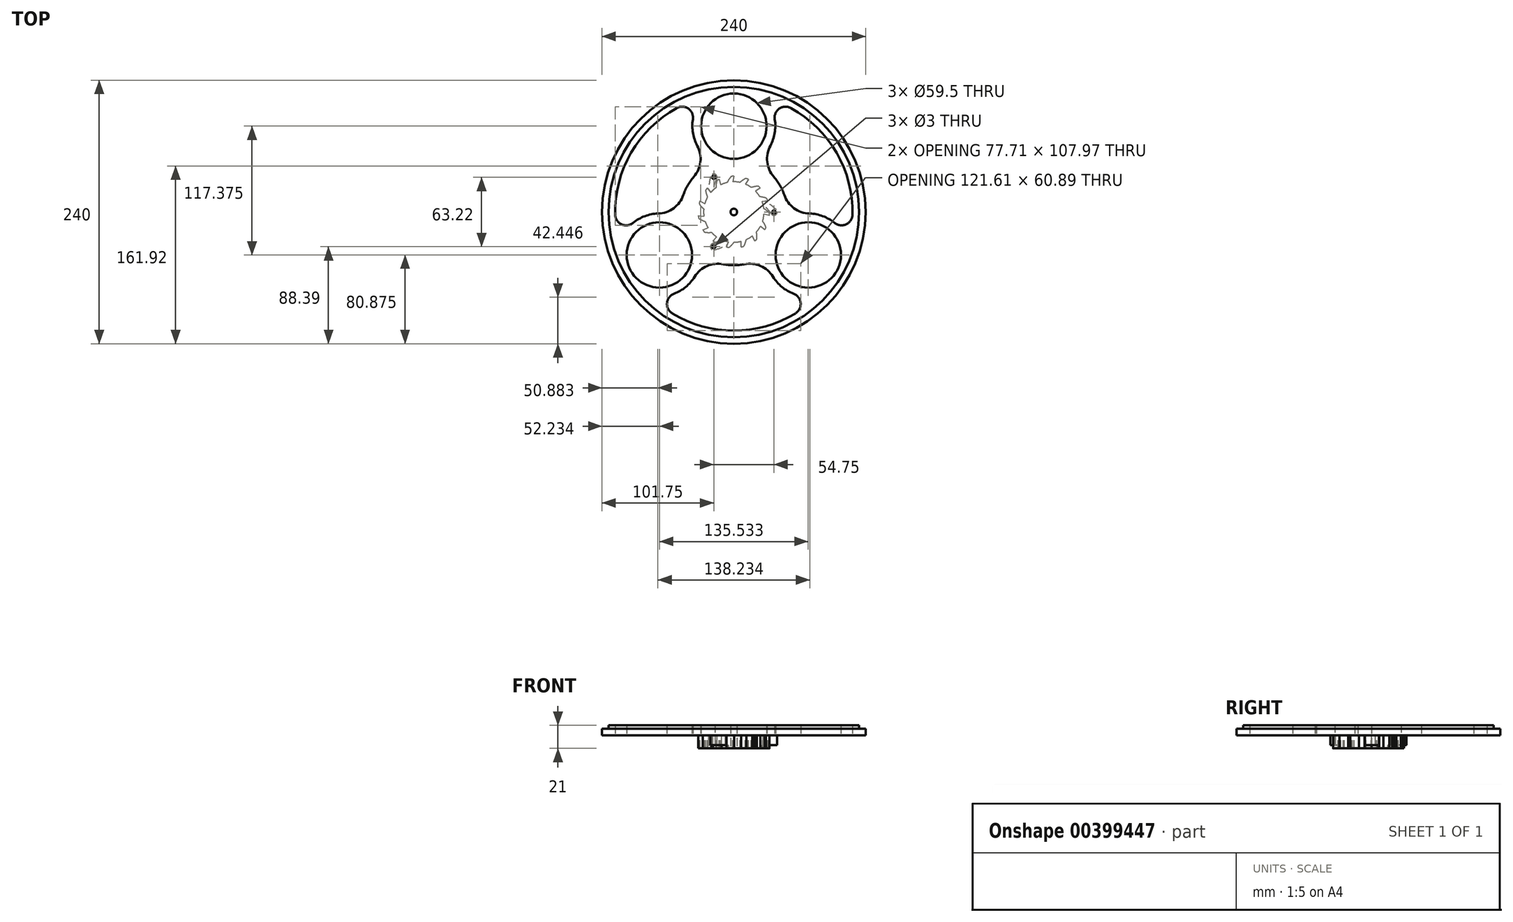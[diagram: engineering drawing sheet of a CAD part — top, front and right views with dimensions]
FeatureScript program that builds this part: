
annotation { "Feature Type Name" : "Feature", "Feature Type Description" : "" }
export const myFeature = defineFeature(function(context is Context, id is Id, definition is map)
    precondition{}
    {
        {
            var Q0;
            Q0=qCreatedBy(makeId("Top.planeOp"),FACE);
            var sketch = newSketch(context, id + "F0", { "sketchPlane" : qUnion([Q0])});
            skCircle(sketch, "E0", {"center": v(0, 0) * mm, "radius": 120 * mm});
            skArc(sketch, "E1", {"start": v(-36.45, 32) * mm, "mid": v(-42, 24.25) * mm, "end": v(-45.93, 15.57) * mm});
            skArc(sketch, "E2", {"start": v(-51.94, 94.7) * mm, "mid": v(-93.53, 54) * mm, "end": v(-107.97, -2.37) * mm});
            skCircle(sketch, "E3", {"center": v(0, 78.25) * mm, "radius": 29.75 * mm});
            skCircle(sketch, "E4", {"center": v(67.77, -39.12) * mm, "radius": 29.75 * mm});
            skCircle(sketch, "E5", {"center": v(-67.77, -39.13) * mm, "radius": 29.75 * mm});
            skLineSegment(sketch, "E6", {"start": v(0, 78.25) * mm, "end": v(-67.77, -39.13) * mm, "construction": true});
            skLineSegment(sketch, "E7", {"start": v(-67.77, -39.13) * mm, "end": v(67.77, -39.12) * mm, "construction": true});
            skLineSegment(sketch, "E8", {"start": v(67.77, -39.12) * mm, "end": v(0, 78.25) * mm, "construction": true});
            skArc(sketch, "E9", {"start": v(-37.26, 84.32) * mm, "mid": v(-37.23, 72) * mm, "end": v(-33.23, 60.34) * mm});
            skArc(sketch, "E10", {"start": v(-68.87, -1.4) * mm, "mid": v(-80.97, -3.76) * mm, "end": v(-91.65, -9.9) * mm});
            skArc(sketch, "E11", {"start": v(35.64, -58.95) * mm, "mid": v(43.74, -68.24) * mm, "end": v(54.4, -74.43) * mm});
            skArc(sketch, "E12.trimOffspring", {"start": v(33.23, 60.34) * mm, "mid": v(37.23, 72) * mm, "end": v(37.26, 84.32) * mm});
            skArc(sketch, "E13.trimOffspring", {"start": v(45.93, 15.57) * mm, "mid": v(42, 24.25) * mm, "end": v(36.45, 32) * mm});
            skArc(sketch, "E14.trimOffspring", {"start": v(-9.48, -47.56) * mm, "mid": v(0, -48.5) * mm, "end": v(9.48, -47.56) * mm});
            skArc(sketch, "E15.trimOffspring", {"start": v(-56.04, -92.33) * mm, "mid": v(0, -108) * mm, "end": v(56.04, -92.33) * mm});
            skArc(sketch, "E16.trimOffspring", {"start": v(-54.4, -74.43) * mm, "mid": v(-43.74, -68.24) * mm, "end": v(-35.64, -58.95) * mm});
            skArc(sketch, "E17.trimOffspring", {"start": v(107.97, -2.37) * mm, "mid": v(93.53, 54) * mm, "end": v(51.94, 94.7) * mm});
            skArc(sketch, "E18.trimOffspring", {"start": v(91.65, -9.9) * mm, "mid": v(80.97, -3.76) * mm, "end": v(68.87, -1.4) * mm});
            skPoint(sketch, "E19.visualSharp", {"position": v(-27.08, 104.55) * mm});
            skArc(sketch, "E19.filletArc", {"start": v(-37.26, 84.32) * mm, "mid": v(-41.36, 94.09) * mm, "end": v(-51.94, 94.7) * mm});
            skPoint(sketch, "E20.visualSharp", {"position": v(-104.08, -28.82) * mm});
            skArc(sketch, "E20.filletArc", {"start": v(-107.97, -2.37) * mm, "mid": v(-102.16, -11.23) * mm, "end": v(-91.65, -9.9) * mm});
            skPoint(sketch, "E21.visualSharp", {"position": v(27.08, 104.55) * mm});
            skArc(sketch, "E21.filletArc", {"start": v(51.94, 94.7) * mm, "mid": v(41.36, 94.09) * mm, "end": v(37.26, 84.32) * mm});
            skPoint(sketch, "E22.visualSharp", {"position": v(104.08, -28.82) * mm});
            skArc(sketch, "E22.filletArc", {"start": v(91.65, -9.9) * mm, "mid": v(102.16, -11.23) * mm, "end": v(107.97, -2.37) * mm});
            skPoint(sketch, "E23.visualSharp", {"position": v(77, -75.73) * mm});
            skArc(sketch, "E23.filletArc", {"start": v(56.04, -92.33) * mm, "mid": v(60.8, -82.86) * mm, "end": v(54.4, -74.43) * mm});
            skPoint(sketch, "E24.visualSharp", {"position": v(-77, -75.73) * mm});
            skArc(sketch, "E24.filletArc", {"start": v(-54.4, -74.43) * mm, "mid": v(-60.8, -82.86) * mm, "end": v(-56.04, -92.33) * mm});
            skPoint(sketch, "E25.visualSharp", {"position": v(-17.97, 45.05) * mm});
            skArc(sketch, "E25.filletArc", {"start": v(-36.45, 32) * mm, "mid": v(-30.4, 45.66) * mm, "end": v(-33.23, 60.34) * mm});
            skPoint(sketch, "E26.visualSharp", {"position": v(-48, -6.97) * mm});
            skArc(sketch, "E26.filletArc", {"start": v(-68.87, -1.4) * mm, "mid": v(-54.75, 3.5) * mm, "end": v(-45.93, 15.57) * mm});
            skPoint(sketch, "E27.visualSharp", {"position": v(-30.03, -38.08) * mm});
            skArc(sketch, "E27.filletArc", {"start": v(-9.48, -47.56) * mm, "mid": v(-24.35, -49.16) * mm, "end": v(-35.64, -58.95) * mm});
            skPoint(sketch, "E28.visualSharp", {"position": v(30.03, -38.08) * mm});
            skArc(sketch, "E28.filletArc", {"start": v(35.64, -58.95) * mm, "mid": v(24.35, -49.16) * mm, "end": v(9.48, -47.56) * mm});
            skPoint(sketch, "E29.visualSharp", {"position": v(48, -6.97) * mm});
            skArc(sketch, "E29.filletArc", {"start": v(45.93, 15.57) * mm, "mid": v(54.75, 3.5) * mm, "end": v(68.87, -1.4) * mm});
            skPoint(sketch, "E30.visualSharp", {"position": v(17.97, 45.05) * mm});
            skArc(sketch, "E30.filletArc", {"start": v(33.23, 60.34) * mm, "mid": v(30.4, 45.66) * mm, "end": v(36.45, 32) * mm});
            skCircle(sketch, "E31", {"center": v(0, 0) * mm, "radius": 3 * mm});
            skCircle(sketch, "E32", {"center": v(0, 0) * mm, "radius": 48.5 * mm, "construction": true});
            skSolve(sketch);
        }
        {
            var Q0;
            Q0=makeQuery(id+"F0.imprint","IMPRINT",FACE,{"disambiguationData":[TD([[makeQuery(id+"F0.imprint","IMPRINT",EDGE,{"derivedFrom":sQuery(id+"F0.wireOp",EDGE,"E0")}),1.0]])]});
            extrude(context, id + "F1", {"entities" : qUnion([Q0]), "depth" : 9 * mm});
        }
        {
            var Q0;
            Q0=qCreatedBy(makeId("Top.planeOp"),FACE);
            var sketch = newSketch(context, id + "F2", { "sketchPlane" : qUnion([Q0])});
            skArc(sketch, "E33", {"start": v(-5.88, 26.86) * mm, "mid": v(3.4, -27.29) * mm, "end": v(-0.88, 27.49) * mm});
            skCircle(sketch, "E34", {"center": v(0, 0) * mm, "radius": 32.5 * mm, "construction": true});
            skLineSegment(sketch, "E35", {"start": v(0, 32.5) * mm, "end": v(-0.88, 27.49) * mm});
            skArc(sketch, "E36", {"start": v(-3.08, 31.66) * mm, "mid": v(-4.61, 29.34) * mm, "end": v(-5.88, 26.86) * mm});
            skPoint(sketch, "E37", {"position": v(-5.88, 26.86) * mm});
            skCircle(sketch, "E38.0", {"center": v(0, 0) * mm, "radius": 3 * mm});
            skArc(sketch, "E39", {"start": v(-1.57, 32.46) * mm, "mid": v(-0.79, 32.5) * mm, "end": v(0, 32.5) * mm});
            skArc(sketch, "E40.trimOffspring", {"start": v(-1.57, 32.46) * mm, "mid": v(-2.41, 32.23) * mm, "end": v(-3.08, 31.66) * mm});
            skPoint(sketch, "E41.orphan", {"position": v(-2.5, 32.4) * mm});
            skSolve(sketch);
        }
        {
            var Q0;
            Q0=makeQuery(id+"F1.opExtrude","CAP_FACE",FACE,{"disambiguationData":[OSD([sQuery(id+"F0.wireOp",EDGE,"E0"),sQuery(id+"F0.wireOp",EDGE,"E1"),sQuery(id+"F0.wireOp",EDGE,"E2"),sQuery(id+"F0.wireOp",EDGE,"E3"),sQuery(id+"F0.wireOp",EDGE,"E4"),sQuery(id+"F0.wireOp",EDGE,"E5"),sQuery(id+"F0.wireOp",EDGE,"E9"),sQuery(id+"F0.wireOp",EDGE,"E10"),sQuery(id+"F0.wireOp",EDGE,"E11"),sQuery(id+"F0.wireOp",EDGE,"E12.trimOffspring"),sQuery(id+"F0.wireOp",EDGE,"E13.trimOffspring"),sQuery(id+"F0.wireOp",EDGE,"E14.trimOffspring"),sQuery(id+"F0.wireOp",EDGE,"E15.trimOffspring"),sQuery(id+"F0.wireOp",EDGE,"E16.trimOffspring"),sQuery(id+"F0.wireOp",EDGE,"E17.trimOffspring"),sQuery(id+"F0.wireOp",EDGE,"E18.trimOffspring"),sQuery(id+"F0.wireOp",EDGE,"E19.filletArc"),sQuery(id+"F0.wireOp",EDGE,"E20.filletArc"),sQuery(id+"F0.wireOp",EDGE,"E21.filletArc"),sQuery(id+"F0.wireOp",EDGE,"E22.filletArc"),sQuery(id+"F0.wireOp",EDGE,"E23.filletArc"),sQuery(id+"F0.wireOp",EDGE,"E24.filletArc"),sQuery(id+"F0.wireOp",EDGE,"E25.filletArc"),sQuery(id+"F0.wireOp",EDGE,"E26.filletArc"),sQuery(id+"F0.wireOp",EDGE,"E27.filletArc"),sQuery(id+"F0.wireOp",EDGE,"E28.filletArc"),sQuery(id+"F0.wireOp",EDGE,"E29.filletArc"),sQuery(id+"F0.wireOp",EDGE,"E30.filletArc"),sQuery(id+"F0.wireOp",EDGE,"E31")])],"isStart":false});
            var sketch = newSketch(context, id + "F3", { "sketchPlane" : qUnion([Q0])});
            skCircle(sketch, "E42", {"center": v(0, 0) * mm, "radius": 114 * mm});
            skCircle(sketch, "E43.0", {"center": v(0, 0) * mm, "radius": 120 * mm});
            skSolve(sketch);
        }
        {
            var Q0;
            Q0=makeQuery(id+"F3.imprint","IMPRINT",FACE,{"disambiguationData":[TD([[makeQuery(id+"F3.imprint","IMPRINT",EDGE,{"derivedFrom":sQuery(id+"F3.wireOp",EDGE,"E42")}),-1.0]])]});
            extrude(context, id + "F4", {"entities" : qUnion([Q0]), "operationType" : NewBodyOperationType.REMOVE, "oppositeDirection" : true, "depth" : 3 * mm});
        }
        {
            var Q0;
            Q0 = qSketchRegion(id + "F2", true);
            extrude(context, id + "F5", {"entities" : qUnion([Q0]), "oppositeDirection" : true, "depth" : 12 * mm});
        }
        {
            var Q0;
            Q0=makeQuery(id+"F5.opExtrude","SWEPT_BODY",BODY,{"disambiguationData":[OSD([sQuery(id+"F2.wireOp",EDGE,"E33"),sQuery(id+"F2.wireOp",EDGE,"E35"),sQuery(id+"F2.wireOp",EDGE,"E36"),sQuery(id+"F2.wireOp",EDGE,"E38.0")])]});
            var Q1;
            Q1=makeQuery(id+"F5.opExtrude","SWEPT_FACE",FACE,{"disambiguationData":[OSD([sQuery(id+"F2.wireOp",EDGE,"E38.0")])]});
            circularPattern(context, id + "F6", {"operationType" : NewBodyOperationType.ADD, "entities" : qUnion([Q0]), "axis" : qUnion([Q1]), "angle" : 360 * degree, "instanceCount" : 15, "equalSpace" : true});
        }
        {
            var Q0;
            Q0=qCreatedBy(makeId("Top.planeOp"),FACE);
            var sketch = newSketch(context, id + "F7", { "sketchPlane" : qUnion([Q0])});
            skArc(sketch, "E44", {"start": v(-18.4, -28.61) * mm, "mid": v(-13, -27.91) * mm, "end": v(-7.77, -26.38) * mm});
            skArc(sketch, "E45", {"start": v(-18.4, -28.61) * mm, "mid": v(-21.2, -32.1) * mm, "end": v(-17.41, -34.5) * mm});
            skArc(sketch, "E46", {"start": v(-17.41, -34.5) * mm, "mid": v(-11.57, -32.47) * mm, "end": v(-5.97, -29.85) * mm});
            skLineSegment(sketch, "E47", {"start": v(0, 0) * mm, "end": v(-18.25, -31.6) * mm, "construction": true});
            skPoint(sketch, "E48", {"position": v(-7.77, -26.38) * mm});
            skCircle(sketch, "E49", {"center": v(-18.25, -31.6) * mm, "radius": 1.5 * mm});
            skPoint(sketch, "E50", {"position": v(-5.97, -29.85) * mm});
            skCircle(sketch, "E51", {"center": v(0, 0) * mm, "radius": 32.5 * mm, "construction": true});
            skLineSegment(sketch, "E52.0", {"start": v(-5.97, -29.85) * mm, "end": v(-4.85, -27.07) * mm});
            skArc(sketch, "E52.1", {"start": v(-7.77, -26.38) * mm, "mid": v(-6.32, -26.76) * mm, "end": v(-4.85, -27.07) * mm});
            skPoint(sketch, "E53.orphan", {"position": v(-6.76, -31.79) * mm});
            skPoint(sketch, "E54.orphan", {"position": v(-11.03, -25.2) * mm});
            skCircle(sketch, "E55", {"center": v(0, 0) * mm, "radius": 33.5 * mm, "construction": true});
            skSolve(sketch);
        }
        {
            var Q0;
            Q0 = qSketchRegion(id + "F7", true);
            extrude(context, id + "F8", {"entities" : qUnion([Q0]), "oppositeDirection" : true, "depth" : 9 * mm});
        }
        {
            var Q0;
            Q0=makeQuery(id+"F8.opExtrude","SWEPT_BODY",BODY,{"disambiguationData":[OSD([sQuery(id+"F7.wireOp",EDGE,"E44"),sQuery(id+"F7.wireOp",EDGE,"E45"),sQuery(id+"F7.wireOp",EDGE,"E46"),sQuery(id+"F7.wireOp",EDGE,"E49"),sQuery(id+"F7.wireOp",EDGE,"E52.0"),sQuery(id+"F7.wireOp",EDGE,"E52.1")])]});
            var Q1;
            Q1=makeQuery(id+"F5.opExtrude","SWEPT_FACE",FACE,{"disambiguationData":[OSD([sQuery(id+"F2.wireOp",EDGE,"E38.0")])]});
            circularPattern(context, id + "F9", {"operationType" : NewBodyOperationType.ADD, "entities" : qUnion([Q0]), "axis" : qUnion([Q1]), "angle" : 360 * degree, "instanceCount" : 3, "equalSpace" : true});
        }
        {
            var Q0;
            Q0=makeQuery(id+"F1.opExtrude","CAP_FACE",FACE,{"disambiguationData":[OSD([sQuery(id+"F0.wireOp",EDGE,"E0"),sQuery(id+"F0.wireOp",EDGE,"E1"),sQuery(id+"F0.wireOp",EDGE,"E2"),sQuery(id+"F0.wireOp",EDGE,"E3"),sQuery(id+"F0.wireOp",EDGE,"E4"),sQuery(id+"F0.wireOp",EDGE,"E5"),sQuery(id+"F0.wireOp",EDGE,"E9"),sQuery(id+"F0.wireOp",EDGE,"E10"),sQuery(id+"F0.wireOp",EDGE,"E11"),sQuery(id+"F0.wireOp",EDGE,"E12.trimOffspring"),sQuery(id+"F0.wireOp",EDGE,"E13.trimOffspring"),sQuery(id+"F0.wireOp",EDGE,"E14.trimOffspring"),sQuery(id+"F0.wireOp",EDGE,"E15.trimOffspring"),sQuery(id+"F0.wireOp",EDGE,"E16.trimOffspring"),sQuery(id+"F0.wireOp",EDGE,"E17.trimOffspring"),sQuery(id+"F0.wireOp",EDGE,"E18.trimOffspring"),sQuery(id+"F0.wireOp",EDGE,"E19.filletArc"),sQuery(id+"F0.wireOp",EDGE,"E20.filletArc"),sQuery(id+"F0.wireOp",EDGE,"E21.filletArc"),sQuery(id+"F0.wireOp",EDGE,"E22.filletArc"),sQuery(id+"F0.wireOp",EDGE,"E23.filletArc"),sQuery(id+"F0.wireOp",EDGE,"E24.filletArc"),sQuery(id+"F0.wireOp",EDGE,"E25.filletArc"),sQuery(id+"F0.wireOp",EDGE,"E26.filletArc"),sQuery(id+"F0.wireOp",EDGE,"E27.filletArc"),sQuery(id+"F0.wireOp",EDGE,"E28.filletArc"),sQuery(id+"F0.wireOp",EDGE,"E29.filletArc"),sQuery(id+"F0.wireOp",EDGE,"E30.filletArc"),sQuery(id+"F0.wireOp",EDGE,"E31")])],"isStart":true});
            var sketch = newSketch(context, id + "F10", { "sketchPlane" : qUnion([Q0])});
            skCircle(sketch, "E56", {"center": v(0, 0) * mm, "radius": 40.5 * mm});
            skCircle(sketch, "E57", {"center": v(0, 0) * mm, "radius": 48.5 * mm});
            skCircle(sketch, "E58", {"center": v(0, 0) * mm, "radius": 39.5 * mm, "construction": true});
            skSolve(sketch);
        }
        {
            var Q0;
            Q0=qCreatedBy(makeId("Top.planeOp"),FACE);
            var sketch = newSketch(context, id + "F11", { "sketchPlane" : qUnion([Q0])});
            skCircle(sketch, "E59.0", {"center": v(-18.25, 31.6) * mm, "radius": 1.5 * mm});
            skCircle(sketch, "E60.0", {"center": v(-18.25, -31.6) * mm, "radius": 1.5 * mm});
            skCircle(sketch, "E61.0", {"center": v(36.5, 0) * mm, "radius": 1.5 * mm});
            skSolve(sketch);
        }
        {
            var Q0;
            Q0 = qSketchRegion(id + "F11", true);
            extrude(context, id + "F12", {"entities" : qUnion([Q0]), "operationType" : NewBodyOperationType.REMOVE, "endBound" : BoundingType.THROUGH_ALL, "depth" : 25 * mm});
        }
    });
